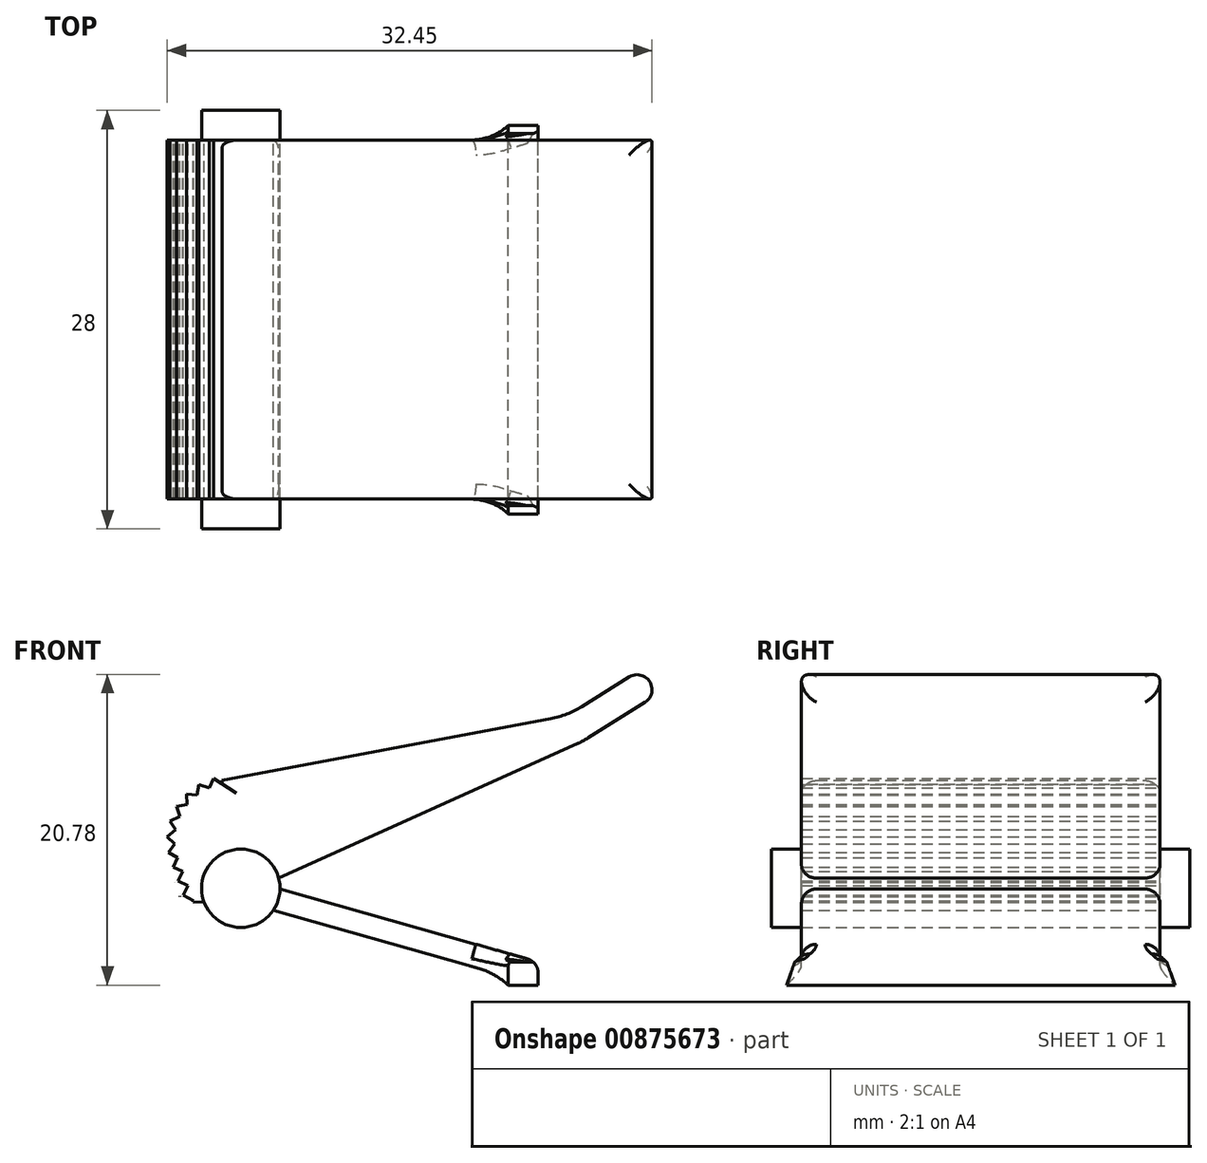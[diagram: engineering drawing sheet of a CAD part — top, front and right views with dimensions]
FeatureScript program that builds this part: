
annotation { "Feature Type Name" : "Feature", "Feature Type Description" : "" }
export const myFeature = defineFeature(function(context is Context, id is Id, definition is map)
    precondition{}
    {
        {
            var Q0;
            Q0=qCreatedBy(makeId("Front.planeOp"),FACE);
            var sketch = newSketch(context, id + "F0", { "sketchPlane" : qUnion([Q0])});
            skPoint(sketch, "E0.center.orphan", {"position": v(0, 0) * mm});
            skArc(sketch, "E1", {"start": v(7.7, 0) * mm, "mid": v(7.68, 0) * mm, "end": v(7.67, 0) * mm});
            skLineSegment(sketch, "E2", {"start": v(26, -5.17) * mm, "end": v(7.7, 0) * mm});
            skLineSegment(sketch, "E3", {"start": v(7.68, 0) * mm, "end": v(28.64, 9.44) * mm});
            skLineSegment(sketch, "E4", {"start": v(29.37, 9.83) * mm, "end": v(34, 12.73) * mm});
            skLineSegment(sketch, "E5", {"start": v(34, 12.73) * mm, "end": v(32.94, 14.42) * mm});
            skLineSegment(sketch, "E6", {"start": v(32.94, 14.42) * mm, "end": v(28.92, 11.9) * mm});
            skArc(sketch, "E7", {"start": v(7.68, 0) * mm, "mid": v(7.68, 0) * mm, "end": v(7.67, 0) * mm});
            skLineSegment(sketch, "E8", {"start": v(34, 12.73) * mm, "end": v(34, -9.77) * mm, "construction": true});
            skLineSegment(sketch, "E9", {"start": v(32.94, 14.42) * mm, "end": v(-3.08, 14.42) * mm, "construction": true});
            skLineSegment(sketch, "E10", {"start": v(29.02, 9.6) * mm, "end": v(27.1, 12.68) * mm, "construction": true});
            skLineSegment(sketch, "E11", {"start": v(26, -6.73) * mm, "end": v(6.25, -1.16) * mm});
            skLineSegment(sketch, "E12", {"start": v(26, -6.73) * mm, "end": v(26, -5.17) * mm});
            skPoint(sketch, "E13.visualSharp", {"position": v(27.96, 11.3) * mm});
            skArc(sketch, "E13.filletArc", {"start": v(26.84, 11.1) * mm, "mid": v(27.92, 11.4) * mm, "end": v(28.92, 11.9) * mm});
            skPoint(sketch, "E14.visualSharp", {"position": v(29.02, 9.6) * mm});
            skArc(sketch, "E14.filletArc", {"start": v(28.64, 9.44) * mm, "mid": v(29.01, 9.62) * mm, "end": v(29.37, 9.83) * mm});
            skLineSegment(sketch, "E15", {"start": v(0, 0) * mm, "end": v(0, 7.97) * mm, "construction": true});
            skLineSegment(sketch, "E16", {"start": v(6.25, -1.16) * mm, "end": v(2.9, -1.17) * mm});
            skPoint(sketch, "E17.visualSharp", {"position": v(0.05, 6.06) * mm});
            skLineSegment(sketch, "E18.1.0", {"start": v(1.25, 2.16) * mm, "end": v(1.74, 2.27) * mm, "construction": true});
            skLineSegment(sketch, "E18.2.0", {"start": v(1.18, 2.68) * mm, "end": v(1.68, 2.73) * mm, "construction": true});
            skLineSegment(sketch, "E18.3.0", {"start": v(1.17, 3.21) * mm, "end": v(1.67, 3.2) * mm, "construction": true});
            skLineSegment(sketch, "E18.4.0", {"start": v(1.23, 3.74) * mm, "end": v(1.73, 3.66) * mm, "construction": true});
            skLineSegment(sketch, "E18.5.0", {"start": v(1.36, 4.25) * mm, "end": v(1.84, 4.12) * mm, "construction": true});
            skLineSegment(sketch, "E18.6.0", {"start": v(1.54, 4.75) * mm, "end": v(2, 4.56) * mm, "construction": true});
            skLineSegment(sketch, "E18.7.0", {"start": v(1.8, 5.22) * mm, "end": v(2.22, 4.97) * mm, "construction": true});
            skLineSegment(sketch, "E18.8.0", {"start": v(2.1, 5.65) * mm, "end": v(2.5, 5.35) * mm, "construction": true});
            skLineSegment(sketch, "E18.9.0", {"start": v(2.45, 6.05) * mm, "end": v(2.8, 5.7) * mm, "construction": true});
            skLineSegment(sketch, "E18.10.0", {"start": v(2.85, 6.4) * mm, "end": v(3.16, 6) * mm, "construction": true});
            skLineSegment(sketch, "E18.11.0", {"start": v(3.3, 6.69) * mm, "end": v(3.55, 6.26) * mm, "construction": true});
            skLineSegment(sketch, "E18.12.0", {"start": v(3.77, 6.92) * mm, "end": v(3.97, 6.47) * mm, "construction": true});
            skLineSegment(sketch, "E18.13.0", {"start": v(4.27, 7.1) * mm, "end": v(4.42, 6.62) * mm, "construction": true});
            skPoint(sketch, "E18.center", {"position": v(5.43, 3) * mm});
            skLineSegment(sketch, "E18.anchor1", {"start": v(5.43, 3) * mm, "end": v(1.16, 1.56) * mm, "construction": true});
            skLineSegment(sketch, "E18.anchor2", {"start": v(5.43, 3) * mm, "end": v(4.74, 7.46) * mm, "construction": true});
            skLineSegment(sketch, "E19", {"start": v(2.02, -0.8) * mm, "end": v(2.02, -0.79) * mm});
            skLineSegment(sketch, "E20", {"start": v(1.68, 0.15) * mm, "end": v(1.67, 0.15) * mm});
            skLineSegment(sketch, "E21.trimOffspring", {"start": v(2.02, -0.79) * mm, "end": v(2.02, -0.8) * mm});
            skLineSegment(sketch, "E22.trimOffspring", {"start": v(1.67, 0.15) * mm, "end": v(1.68, 0.15) * mm});
            skLineSegment(sketch, "E23", {"start": v(1.63, 1.73) * mm, "end": v(1.62, 1.71) * mm});
            skLineSegment(sketch, "E24.trimOffspring", {"start": v(4.82, 6.96) * mm, "end": v(26.84, 11.1) * mm});
            skLineSegment(sketch, "E25.0", {"start": v(2.9, -1.17) * mm, "end": v(2.93, -1.1) * mm});
            skLineSegment(sketch, "E26", {"start": v(2.93, -1.1) * mm, "end": v(2.25, -0.7) * mm});
            skLineSegment(sketch, "E27", {"start": v(2.25, -0.7) * mm, "end": v(2.55, -0.06) * mm});
            skLineSegment(sketch, "E28", {"start": v(2.55, -0.06) * mm, "end": v(1.9, 0.23) * mm});
            skLineSegment(sketch, "E29", {"start": v(1.9, 0.23) * mm, "end": v(2.2, 0.88) * mm});
            skLineSegment(sketch, "E30", {"start": v(2.2, 0.88) * mm, "end": v(1.56, 1.17) * mm});
            skLineSegment(sketch, "E31", {"start": v(1.86, 1.81) * mm, "end": v(1.56, 1.17) * mm});
            skPoint(sketch, "E32.start.orphan", {"position": v(2.69, -1.17) * mm});
            skLineSegment(sketch, "E33.trimOffspring", {"start": v(2.02, -0.79) * mm, "end": v(2.02, -0.79) * mm});
            skLineSegment(sketch, "E34.trimOffspring", {"start": v(1.67, 0.15) * mm, "end": v(1.67, 0.15) * mm});
            skArc(sketch, "E35", {"start": v(4.83, 6.96) * mm, "mid": v(2, 5.1) * mm, "end": v(1.63, 1.73) * mm, "construction": true});
            skArc(sketch, "E36.0", {"start": v(4.8, 7.2) * mm, "mid": v(1.8, 5.23) * mm, "end": v(1.4, 1.65) * mm, "construction": true});
            skArc(sketch, "E37.0", {"start": v(4.87, 6.71) * mm, "mid": v(2.22, 4.96) * mm, "end": v(1.86, 1.8) * mm, "construction": true});
            skPoint(sketch, "E38.orphan", {"position": v(4.34, 6.86) * mm});
            skPoint(sketch, "E39.orphan", {"position": v(3.42, 6.47) * mm});
            skPoint(sketch, "E40.orphan", {"position": v(2.63, 5.87) * mm});
            skPoint(sketch, "E41.orphan", {"position": v(2, 5.1) * mm});
            skPoint(sketch, "E42.orphan", {"position": v(1.6, 4.19) * mm});
            skPoint(sketch, "E43.orphan", {"position": v(1.42, 3.2) * mm});
            skPoint(sketch, "E44.orphan", {"position": v(1.5, 2.21) * mm});
            skLineSegment(sketch, "E45", {"start": v(4.87, 6.71) * mm, "end": v(4.83, 6.96) * mm});
            skLineSegment(sketch, "E46", {"start": v(4.87, 6.71) * mm, "end": v(4.27, 7.1) * mm});
            skLineSegment(sketch, "E47", {"start": v(4.27, 7.1) * mm, "end": v(3.97, 6.47) * mm});
            skLineSegment(sketch, "E48", {"start": v(3.97, 6.47) * mm, "end": v(3.3, 6.69) * mm});
            skLineSegment(sketch, "E49", {"start": v(3.3, 6.69) * mm, "end": v(3.16, 6) * mm});
            skLineSegment(sketch, "E50", {"start": v(3.16, 6) * mm, "end": v(2.45, 6.05) * mm});
            skLineSegment(sketch, "E51", {"start": v(2.45, 6.05) * mm, "end": v(2.5, 5.35) * mm});
            skLineSegment(sketch, "E52", {"start": v(2.5, 5.35) * mm, "end": v(1.8, 5.22) * mm});
            skLineSegment(sketch, "E53", {"start": v(1.8, 5.22) * mm, "end": v(2, 4.56) * mm});
            skLineSegment(sketch, "E54", {"start": v(2, 4.56) * mm, "end": v(1.36, 4.25) * mm});
            skLineSegment(sketch, "E55", {"start": v(1.36, 4.25) * mm, "end": v(1.73, 3.66) * mm});
            skLineSegment(sketch, "E56", {"start": v(1.73, 3.66) * mm, "end": v(1.17, 3.21) * mm});
            skLineSegment(sketch, "E57", {"start": v(1.17, 3.21) * mm, "end": v(1.68, 2.73) * mm});
            skLineSegment(sketch, "E58", {"start": v(1.68, 2.73) * mm, "end": v(1.25, 2.16) * mm});
            skLineSegment(sketch, "E59", {"start": v(1.25, 2.16) * mm, "end": v(1.86, 1.8) * mm});
            skSolve(sketch);
        }
        {
            var Q0;
            Q0 = qSketchRegion(id + "F0", true);
            extrude(context, id + "F1", {"entities" : qUnion([Q0]), "depth" : 24 * mm, "offsetDistance" : 25 * mm});
        }
        {
            var Q0;
            Q0=qCreatedBy(makeId("Front.planeOp"),FACE);
            cPlane(context, id + "F2", {"entities" : qUnion([Q0]), "cplaneType" : CPlaneType.OFFSET, "offset" : 12 * mm, "width" : 150 * mm, "height" : 150 * mm});
        }
        {
            var Q0;
            Q0=qCreatedBy(id+"F2.planeOp",FACE);
            var sketch = newSketch(context, id + "F3", { "sketchPlane" : qUnion([Q0])});
            skCircle(sketch, "E60", {"center": v(6.1, -0.25) * mm, "radius": 2.62 * mm});
            skSolve(sketch);
        }
        {
            var Q0;
            Q0 = qSketchRegion(id + "F3", true);
            extrude(context, id + "F4", {"entities" : qUnion([Q0]), "operationType" : NewBodyOperationType.ADD, "endBound" : BoundingType.SYMMETRIC, "depth" : 28 * mm, "offsetDistance" : 25 * mm});
        }
        {
            var Q0;
            Q0=makeQuery(id+"F1.opExtrude","SWEPT_FACE",FACE,{"disambiguationData":[OSD([sQuery(id+"F0.wireOp",EDGE,"E12")])]});
            var sketch = newSketch(context, id + "F5", { "sketchPlane" : qUnion([Q0])});
            skLineSegment(sketch, "E61", {"start": v(-24, -5.17) * mm, "end": v(-24.45, -5.17) * mm});
            skLineSegment(sketch, "E62", {"start": v(-24.45, -5.17) * mm, "end": v(-25, -6.73) * mm});
            skLineSegment(sketch, "E63", {"start": v(-25, -6.73) * mm, "end": v(-24, -6.73) * mm});
            skLineSegment(sketch, "E64", {"start": v(-24, -6.73) * mm, "end": v(-24, -5.17) * mm});
            skLineSegment(sketch, "E65", {"start": v(0, -5.17) * mm, "end": v(0.45, -5.17) * mm});
            skLineSegment(sketch, "E66", {"start": v(0.45, -5.17) * mm, "end": v(1, -6.73) * mm});
            skLineSegment(sketch, "E67", {"start": v(1, -6.73) * mm, "end": v(0, -6.73) * mm});
            skSolve(sketch);
        }
        {
            var Q0;
            Q0 = qSketchRegion(id + "F5", true);
            var Q1;
            Q1=makeQuery(id+"F5.imprint","IMPRINT",FACE,{"disambiguationData":[TD([[makeQuery(id+"F5.imprint","IMPRINT",EDGE,{"derivedFrom":sQuery(id+"F5.wireOp",EDGE,"E65")}),-1.0]])]});
            var Q2;
            Q2=makeQuery(id+"F5.imprint","IMPRINT",FACE,{"disambiguationData":[TD([[makeQuery(id+"F5.imprint","IMPRINT",EDGE,{"derivedFrom":sQuery(id+"F5.wireOp",EDGE,"E64")}),-1.0]])]});
            extrude(context, id + "F6", {"entities" : qUnion([Q0, Q1, Q2]), "operationType" : NewBodyOperationType.ADD, "oppositeDirection" : true, "depth" : 2 * mm, "offsetDistance" : 25 * mm});
        }
        {
            var Q0;
            {var subQ0=sQuery(id+"F0.wireOp",EDGE,"E11");Q0=makeQuery(id+"F6.boolean.opBoolean","INTERSECT",EDGE,{"derivedFrom":[makeQuery(id+"F1.opExtrude","SWEPT_FACE",FACE,{"disambiguationData":[OSD([subQ0])]}),makeQuery(id+"F6.opExtrude","CAP_FACE",FACE,{"disambiguationData":[OSD([sQuery(id+"F0.wireOp",EDGE,"E2"),subQ0,sQuery(id+"F0.wireOp",EDGE,"E12"),sQuery(id+"F5.wireOp",EDGE,"E61"),sQuery(id+"F5.wireOp",EDGE,"E62"),sQuery(id+"F5.wireOp",EDGE,"E63"),sQuery(id+"F5.wireOp",EDGE,"E65"),sQuery(id+"F5.wireOp",EDGE,"E66"),sQuery(id+"F5.wireOp",EDGE,"E67")])],"isStart":false})]});}
            fillet(context, id + "F7", {"entities" : qUnion([Q0]), "radius" : 5 * mm, "tangentPropagation" : true, "allowEdgeOverflow" : false});
        }
        {
            var Q0;
            {var subQ0=sQuery(id+"F0.wireOp",EDGE,"E12");var subQ1=sQuery(id+"F0.wireOp",EDGE,"E11");var subQ2=sQuery(id+"F0.wireOp",EDGE,"E2");Q0=makeQuery(id+"F6.boolean.opBoolean","INTERSECT",EDGE,{"derivedFrom":[makeQuery(id+"F4.boolean.opBoolean","SPLIT",FACE,{"disambiguationData":[TD([makeQuery(id+"F1.opExtrude","SWEPT_FACE",FACE,{"disambiguationData":[OSD([subQ2])]})])],"derivedFrom":makeQuery(id+"F1.opExtrude","CAP_FACE",FACE,{"disambiguationData":[OSD([sQuery(id+"F0.wireOp",EDGE,"E1"),subQ2,sQuery(id+"F0.wireOp",EDGE,"E3"),sQuery(id+"F0.wireOp",EDGE,"E4"),sQuery(id+"F0.wireOp",EDGE,"E5"),sQuery(id+"F0.wireOp",EDGE,"E6"),sQuery(id+"F0.wireOp",EDGE,"E7"),subQ1,subQ0,sQuery(id+"F0.wireOp",EDGE,"E13.filletArc"),sQuery(id+"F0.wireOp",EDGE,"E14.filletArc"),sQuery(id+"F0.wireOp",EDGE,"E16"),sQuery(id+"F0.wireOp",EDGE,"E24.trimOffspring"),sQuery(id+"F0.wireOp",EDGE,"E25.0"),sQuery(id+"F0.wireOp",EDGE,"E26"),sQuery(id+"F0.wireOp",EDGE,"E27"),sQuery(id+"F0.wireOp",EDGE,"E28"),sQuery(id+"F0.wireOp",EDGE,"E29"),sQuery(id+"F0.wireOp",EDGE,"E30"),sQuery(id+"F0.wireOp",EDGE,"E31"),sQuery(id+"F0.wireOp",EDGE,"E45"),sQuery(id+"F0.wireOp",EDGE,"E46"),sQuery(id+"F0.wireOp",EDGE,"E47"),sQuery(id+"F0.wireOp",EDGE,"E48"),sQuery(id+"F0.wireOp",EDGE,"E49"),sQuery(id+"F0.wireOp",EDGE,"E50"),sQuery(id+"F0.wireOp",EDGE,"E51"),sQuery(id+"F0.wireOp",EDGE,"E52"),sQuery(id+"F0.wireOp",EDGE,"E53"),sQuery(id+"F0.wireOp",EDGE,"E54"),sQuery(id+"F0.wireOp",EDGE,"E55"),sQuery(id+"F0.wireOp",EDGE,"E56"),sQuery(id+"F0.wireOp",EDGE,"E57"),sQuery(id+"F0.wireOp",EDGE,"E58"),sQuery(id+"F0.wireOp",EDGE,"E59")])],"isStart":true})}),makeQuery(id+"F6.opExtrude","CAP_FACE",FACE,{"disambiguationData":[OSD([subQ2,subQ1,subQ0,sQuery(id+"F5.wireOp",EDGE,"E61"),sQuery(id+"F5.wireOp",EDGE,"E62"),sQuery(id+"F5.wireOp",EDGE,"E63"),sQuery(id+"F5.wireOp",EDGE,"E65"),sQuery(id+"F5.wireOp",EDGE,"E66"),sQuery(id+"F5.wireOp",EDGE,"E67")])],"isStart":false})]});}
            var Q1;
            {var subQ0=sQuery(id+"F0.wireOp",EDGE,"E12");var subQ1=sQuery(id+"F0.wireOp",EDGE,"E11");var subQ2=sQuery(id+"F0.wireOp",EDGE,"E2");Q1=makeQuery(id+"F6.boolean.opBoolean","INTERSECT",EDGE,{"derivedFrom":[makeQuery(id+"F4.boolean.opBoolean","SPLIT",FACE,{"disambiguationData":[TD([makeQuery(id+"F1.opExtrude","SWEPT_FACE",FACE,{"disambiguationData":[OSD([subQ2])]})])],"derivedFrom":makeQuery(id+"F1.opExtrude","CAP_FACE",FACE,{"disambiguationData":[OSD([sQuery(id+"F0.wireOp",EDGE,"E1"),subQ2,sQuery(id+"F0.wireOp",EDGE,"E3"),sQuery(id+"F0.wireOp",EDGE,"E4"),sQuery(id+"F0.wireOp",EDGE,"E5"),sQuery(id+"F0.wireOp",EDGE,"E6"),sQuery(id+"F0.wireOp",EDGE,"E7"),subQ1,subQ0,sQuery(id+"F0.wireOp",EDGE,"E13.filletArc"),sQuery(id+"F0.wireOp",EDGE,"E14.filletArc"),sQuery(id+"F0.wireOp",EDGE,"E16"),sQuery(id+"F0.wireOp",EDGE,"E24.trimOffspring"),sQuery(id+"F0.wireOp",EDGE,"E25.0"),sQuery(id+"F0.wireOp",EDGE,"E26"),sQuery(id+"F0.wireOp",EDGE,"E27"),sQuery(id+"F0.wireOp",EDGE,"E28"),sQuery(id+"F0.wireOp",EDGE,"E29"),sQuery(id+"F0.wireOp",EDGE,"E30"),sQuery(id+"F0.wireOp",EDGE,"E31"),sQuery(id+"F0.wireOp",EDGE,"E45"),sQuery(id+"F0.wireOp",EDGE,"E46"),sQuery(id+"F0.wireOp",EDGE,"E47"),sQuery(id+"F0.wireOp",EDGE,"E48"),sQuery(id+"F0.wireOp",EDGE,"E49"),sQuery(id+"F0.wireOp",EDGE,"E50"),sQuery(id+"F0.wireOp",EDGE,"E51"),sQuery(id+"F0.wireOp",EDGE,"E52"),sQuery(id+"F0.wireOp",EDGE,"E53"),sQuery(id+"F0.wireOp",EDGE,"E54"),sQuery(id+"F0.wireOp",EDGE,"E55"),sQuery(id+"F0.wireOp",EDGE,"E56"),sQuery(id+"F0.wireOp",EDGE,"E57"),sQuery(id+"F0.wireOp",EDGE,"E58"),sQuery(id+"F0.wireOp",EDGE,"E59")])],"isStart":false})}),makeQuery(id+"F6.opExtrude","CAP_FACE",FACE,{"disambiguationData":[OSD([subQ2,subQ1,subQ0,sQuery(id+"F5.wireOp",EDGE,"E61"),sQuery(id+"F5.wireOp",EDGE,"E62"),sQuery(id+"F5.wireOp",EDGE,"E63"),sQuery(id+"F5.wireOp",EDGE,"E65"),sQuery(id+"F5.wireOp",EDGE,"E66"),sQuery(id+"F5.wireOp",EDGE,"E67")])],"isStart":false})]});}
            fillet(context, id + "F8", {"entities" : qUnion([Q0, Q1]), "radius" : 5 * mm, "tangentPropagation" : true, "allowEdgeOverflow" : false});
        }
        {
            var Q0;
            {var subQ0=sQuery(id+"F0.wireOp",EDGE,"E12");var subQ1=sQuery(id+"F0.wireOp",EDGE,"E2");var subQ2=sQuery(id+"F0.wireOp",EDGE,"E11");Q0=makeQuery(id+"F6.boolean.opBoolean","INTERSECT",EDGE,{"derivedFrom":[makeQuery(id+"F4.boolean.opBoolean","SPLIT",FACE,{"disambiguationData":[TD([makeQuery(id+"F1.opExtrude","SWEPT_FACE",FACE,{"disambiguationData":[OSD([subQ1])]})])],"derivedFrom":makeQuery(id+"F1.opExtrude","CAP_FACE",FACE,{"disambiguationData":[OSD([sQuery(id+"F0.wireOp",EDGE,"E1"),subQ1,sQuery(id+"F0.wireOp",EDGE,"E3"),sQuery(id+"F0.wireOp",EDGE,"E4"),sQuery(id+"F0.wireOp",EDGE,"E5"),sQuery(id+"F0.wireOp",EDGE,"E6"),sQuery(id+"F0.wireOp",EDGE,"E7"),subQ2,subQ0,sQuery(id+"F0.wireOp",EDGE,"E13.filletArc"),sQuery(id+"F0.wireOp",EDGE,"E14.filletArc"),sQuery(id+"F0.wireOp",EDGE,"E16"),sQuery(id+"F0.wireOp",EDGE,"E24.trimOffspring"),sQuery(id+"F0.wireOp",EDGE,"E25.0"),sQuery(id+"F0.wireOp",EDGE,"E26"),sQuery(id+"F0.wireOp",EDGE,"E27"),sQuery(id+"F0.wireOp",EDGE,"E28"),sQuery(id+"F0.wireOp",EDGE,"E29"),sQuery(id+"F0.wireOp",EDGE,"E30"),sQuery(id+"F0.wireOp",EDGE,"E31"),sQuery(id+"F0.wireOp",EDGE,"E45"),sQuery(id+"F0.wireOp",EDGE,"E46"),sQuery(id+"F0.wireOp",EDGE,"E47"),sQuery(id+"F0.wireOp",EDGE,"E48"),sQuery(id+"F0.wireOp",EDGE,"E49"),sQuery(id+"F0.wireOp",EDGE,"E50"),sQuery(id+"F0.wireOp",EDGE,"E51"),sQuery(id+"F0.wireOp",EDGE,"E52"),sQuery(id+"F0.wireOp",EDGE,"E53"),sQuery(id+"F0.wireOp",EDGE,"E54"),sQuery(id+"F0.wireOp",EDGE,"E55"),sQuery(id+"F0.wireOp",EDGE,"E56"),sQuery(id+"F0.wireOp",EDGE,"E57"),sQuery(id+"F0.wireOp",EDGE,"E58"),sQuery(id+"F0.wireOp",EDGE,"E59")])],"isStart":false})}),makeQuery(id+"F6.opExtrude","SWEPT_FACE",FACE,{"disambiguationData":[OSD([subQ1,subQ0,sQuery(id+"F5.wireOp",EDGE,"E61"),sQuery(id+"F5.wireOp",EDGE,"E65")])]})]});}
            var Q1;
            {var subQ0=sQuery(id+"F0.wireOp",EDGE,"E12");var subQ1=sQuery(id+"F0.wireOp",EDGE,"E2");var subQ2=sQuery(id+"F0.wireOp",EDGE,"E11");Q1=makeQuery(id+"F6.boolean.opBoolean","INTERSECT",EDGE,{"derivedFrom":[makeQuery(id+"F4.boolean.opBoolean","SPLIT",FACE,{"disambiguationData":[TD([makeQuery(id+"F1.opExtrude","SWEPT_FACE",FACE,{"disambiguationData":[OSD([subQ1])]})])],"derivedFrom":makeQuery(id+"F1.opExtrude","CAP_FACE",FACE,{"disambiguationData":[OSD([sQuery(id+"F0.wireOp",EDGE,"E1"),subQ1,sQuery(id+"F0.wireOp",EDGE,"E3"),sQuery(id+"F0.wireOp",EDGE,"E4"),sQuery(id+"F0.wireOp",EDGE,"E5"),sQuery(id+"F0.wireOp",EDGE,"E6"),sQuery(id+"F0.wireOp",EDGE,"E7"),subQ2,subQ0,sQuery(id+"F0.wireOp",EDGE,"E13.filletArc"),sQuery(id+"F0.wireOp",EDGE,"E14.filletArc"),sQuery(id+"F0.wireOp",EDGE,"E16"),sQuery(id+"F0.wireOp",EDGE,"E24.trimOffspring"),sQuery(id+"F0.wireOp",EDGE,"E25.0"),sQuery(id+"F0.wireOp",EDGE,"E26"),sQuery(id+"F0.wireOp",EDGE,"E27"),sQuery(id+"F0.wireOp",EDGE,"E28"),sQuery(id+"F0.wireOp",EDGE,"E29"),sQuery(id+"F0.wireOp",EDGE,"E30"),sQuery(id+"F0.wireOp",EDGE,"E31"),sQuery(id+"F0.wireOp",EDGE,"E45"),sQuery(id+"F0.wireOp",EDGE,"E46"),sQuery(id+"F0.wireOp",EDGE,"E47"),sQuery(id+"F0.wireOp",EDGE,"E48"),sQuery(id+"F0.wireOp",EDGE,"E49"),sQuery(id+"F0.wireOp",EDGE,"E50"),sQuery(id+"F0.wireOp",EDGE,"E51"),sQuery(id+"F0.wireOp",EDGE,"E52"),sQuery(id+"F0.wireOp",EDGE,"E53"),sQuery(id+"F0.wireOp",EDGE,"E54"),sQuery(id+"F0.wireOp",EDGE,"E55"),sQuery(id+"F0.wireOp",EDGE,"E56"),sQuery(id+"F0.wireOp",EDGE,"E57"),sQuery(id+"F0.wireOp",EDGE,"E58"),sQuery(id+"F0.wireOp",EDGE,"E59")])],"isStart":true})}),makeQuery(id+"F6.opExtrude","SWEPT_FACE",FACE,{"disambiguationData":[OSD([subQ1,subQ0,sQuery(id+"F5.wireOp",EDGE,"E61"),sQuery(id+"F5.wireOp",EDGE,"E65")])]})]});}
            fillet(context, id + "F9", {"entities" : qUnion([Q0, Q1]), "radius" : 1 * mm, "tangentPropagation" : true, "allowEdgeOverflow" : false});
        }
        {
            var Q0;
            Q0=makeQuery(id+"F1.opExtrude","SWEPT_EDGE",EDGE,{"disambiguationData":[OSD([sQuery(id+"F0.wireOp",EDGE,"E2"),sQuery(id+"F0.wireOp",EDGE,"E12")])]});
            var Q1;
            Q1=makeQuery(id+"F1.opExtrude","CAP_EDGE",EDGE,{"disambiguationData":[OSD([sQuery(id+"F0.wireOp",EDGE,"E2")])],"isStart":true});
            var Q2;
            Q2=makeQuery(id+"F1.opExtrude","CAP_EDGE",EDGE,{"disambiguationData":[OSD([sQuery(id+"F0.wireOp",EDGE,"E2")])],"isStart":false});
            var Q3;
            Q3=makeQuery(id+"F1.opExtrude","SWEPT_EDGE",EDGE,{"disambiguationData":[OSD([sQuery(id+"F0.wireOp",EDGE,"E5"),sQuery(id+"F0.wireOp",EDGE,"E6")])]});
            var Q4;
            Q4=makeQuery(id+"F1.opExtrude","SWEPT_EDGE",EDGE,{"disambiguationData":[OSD([sQuery(id+"F0.wireOp",EDGE,"E4"),sQuery(id+"F0.wireOp",EDGE,"E5")])]});
            var Q5;
            Q5=makeQuery(id+"F1.opExtrude","CAP_EDGE",EDGE,{"disambiguationData":[OSD([sQuery(id+"F0.wireOp",EDGE,"E24.trimOffspring")])],"isStart":false});
            var Q6;
            Q6=makeQuery(id+"F1.opExtrude","CAP_EDGE",EDGE,{"disambiguationData":[OSD([sQuery(id+"F0.wireOp",EDGE,"E3")])],"isStart":false});
            var Q7;
            Q7=makeQuery(id+"F1.opExtrude","CAP_EDGE",EDGE,{"disambiguationData":[OSD([sQuery(id+"F0.wireOp",EDGE,"E24.trimOffspring")])],"isStart":true});
            var Q8;
            Q8=makeQuery(id+"F1.opExtrude","CAP_EDGE",EDGE,{"disambiguationData":[OSD([sQuery(id+"F0.wireOp",EDGE,"E3")])],"isStart":true});
            fillet(context, id + "F10", {"entities" : qUnion([Q0, Q1, Q2, Q3, Q4, Q5, Q6, Q7, Q8]), "radius" : 1 * mm, "tangentPropagation" : true, "allowEdgeOverflow" : false});
        }
    });
